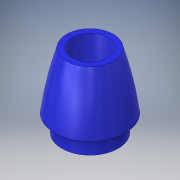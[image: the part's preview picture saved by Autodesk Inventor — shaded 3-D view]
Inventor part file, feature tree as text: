
AUTODESK INVENTOR PART (.ipt)
format: ipt  version: 2018 (Build 220112000, 112)  size: 140,800 bytes
history: native  units: in
note: dims shown in document units (in); Inventor stores cm internally (conversion verified against a paired STEP export)
features: revolve x1, sketch x1
ambient origin geometry x8: Origin, YZ Plane, XZ Plane, XY Plane, X Axis, Y Axis, Z Axis, Center Point
bodies: Solid1 (feature_tree)
feature tree (2):
  revolve  "Revolution1"  [1 undecoded]
  sketch  "Sketch1"  dims[d0=1.5625in d1=5.0in d3=14.0in d4=90.0deg d5=1.5in d6=1.5in d7=2.5in d9=0.75in d10=0.25in d11=0.75in d12=0.25in]
note: 1 required parameter value undecoded (feature->parameter linkage not recoverable at this tier; creation-order binding heuristic only, values carry confidence <= 0.55)
